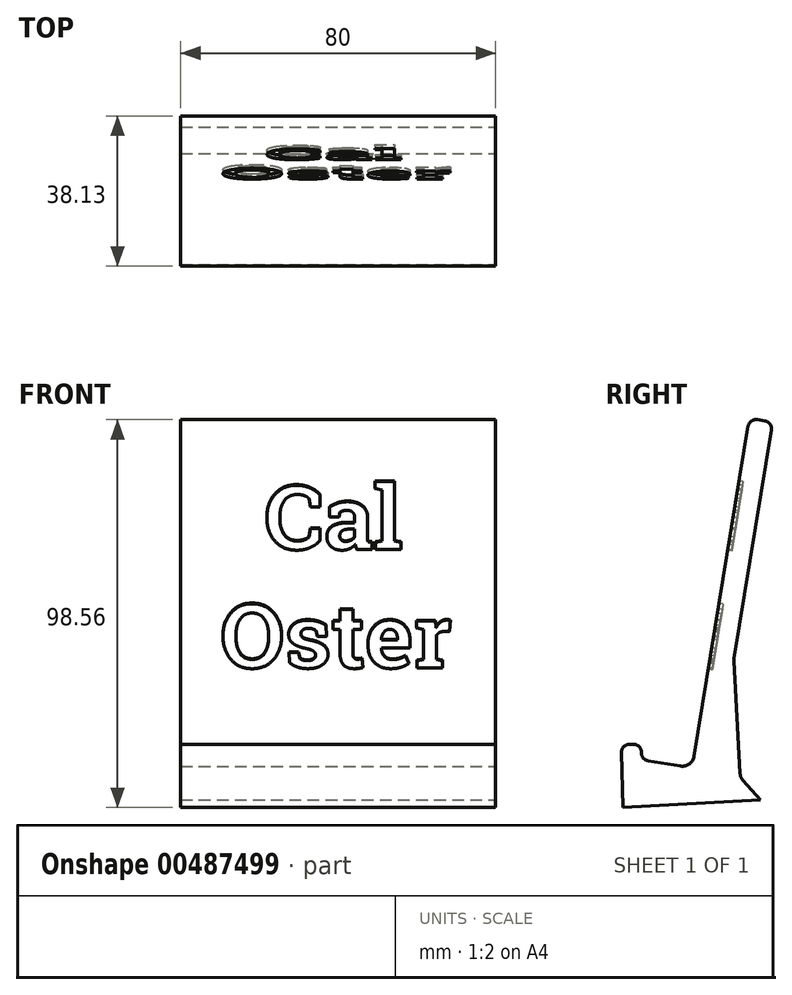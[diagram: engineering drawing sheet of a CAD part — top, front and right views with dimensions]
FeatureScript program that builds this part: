
annotation { "Feature Type Name" : "Feature", "Feature Type Description" : "" }
export const myFeature = defineFeature(function(context is Context, id is Id, definition is map)
    precondition{}
    {
        {
            var Q0;
            Q0=qCreatedBy(makeId("Right.planeOp"),FACE);
            var sketch = newSketch(context, id + "F0", { "sketchPlane" : qUnion([Q0])});
            skLineSegment(sketch, "E0", {"start": v(-4.82, -56.69) * mm, "end": v(-24.14, 31.22) * mm});
            skLineSegment(sketch, "E1", {"start": v(-4.82, -56.69) * mm, "end": v(7.88, -53.9) * mm});
            skLineSegment(sketch, "E2", {"start": v(7.88, -53.9) * mm, "end": v(7.88, -49.9) * mm});
            skLineSegment(sketch, "E3.0", {"start": v(-16.88, -29.77) * mm, "end": v(-30, 29.93) * mm});
            skLineSegment(sketch, "E4", {"start": v(-24.14, 31.22) * mm, "end": v(-30, 29.93) * mm});
            skLineSegment(sketch, "E5", {"start": v(7.88, -49.9) * mm, "end": v(12.88, -49.76) * mm});
            skLineSegment(sketch, "E6", {"start": v(-16.88, -29.77) * mm, "end": v(-16.88, -59.77) * mm});
            skLineSegment(sketch, "E7", {"start": v(12.88, -49.76) * mm, "end": v(13.31, -65.75) * mm});
            skLineSegment(sketch, "E8", {"start": v(-21.69, -65.75) * mm, "end": v(-16.88, -59.77) * mm});
            skLineSegment(sketch, "E9", {"start": v(13.31, -65.75) * mm, "end": v(-21.69, -65.75) * mm});
            skSolve(sketch);
        }
        {
            var Q0;
            Q0=makeQuery(id+"F0.imprint","IMPRINT",FACE,{"disambiguationData":[TD([[makeQuery(id+"F0.imprint","IMPRINT",EDGE,{"derivedFrom":sQuery(id+"F0.wireOp",EDGE,"E0")}),1.0]])]});
            extrude(context, id + "F1", {"entities" : qUnion([Q0]), "depth" : 80 * mm});
        }
        {
            var Q0;
            Q0=makeQuery(id+"F1.opExtrude","SWEPT_EDGE",EDGE,{"disambiguationData":[OSD([sQuery(id+"F0.wireOp",EDGE,"E3.0"),sQuery(id+"F0.wireOp",EDGE,"E4")])]});
            fillet(context, id + "F2", {"entities" : qUnion([Q0]), "radius" : 2 * mm, "tangentPropagation" : true, "allowEdgeOverflow" : false});
        }
        {
            var Q0;
            Q0=makeQuery(id+"F1.opExtrude","SWEPT_EDGE",EDGE,{"disambiguationData":[OSD([sQuery(id+"F0.wireOp",EDGE,"E0"),sQuery(id+"F0.wireOp",EDGE,"E4")])]});
            fillet(context, id + "F3", {"entities" : qUnion([Q0]), "radius" : 2 * mm, "tangentPropagation" : true, "allowEdgeOverflow" : false});
        }
        {
            var Q0;
            Q0=makeQuery(id+"F1.opExtrude","SWEPT_EDGE",EDGE,{"disambiguationData":[OSD([sQuery(id+"F0.wireOp",EDGE,"E0"),sQuery(id+"F0.wireOp",EDGE,"E1")])]});
            fillet(context, id + "F4", {"entities" : qUnion([Q0]), "radius" : 3 * mm, "tangentPropagation" : true, "allowEdgeOverflow" : false});
        }
        {
            var Q0;
            Q0=makeQuery(id+"F1.opExtrude","SWEPT_EDGE",EDGE,{"disambiguationData":[OSD([sQuery(id+"F0.wireOp",EDGE,"E1"),sQuery(id+"F0.wireOp",EDGE,"E2")])]});
            fillet(context, id + "F5", {"entities" : qUnion([Q0]), "radius" : 2 * mm, "tangentPropagation" : true, "allowEdgeOverflow" : false});
        }
        {
            var Q0;
            Q0=makeQuery(id+"F1.opExtrude","SWEPT_EDGE",EDGE,{"disambiguationData":[OSD([sQuery(id+"F0.wireOp",EDGE,"E5"),sQuery(id+"F0.wireOp",EDGE,"E7")])]});
            fillet(context, id + "F6", {"entities" : qUnion([Q0]), "radius" : 2 * mm, "tangentPropagation" : true, "allowEdgeOverflow" : false});
        }
        {
            var Q0;
            Q0=makeQuery(id+"F1.opExtrude","SWEPT_EDGE",EDGE,{"disambiguationData":[OSD([sQuery(id+"F0.wireOp",EDGE,"E2"),sQuery(id+"F0.wireOp",EDGE,"E5")])]});
            fillet(context, id + "F7", {"entities" : qUnion([Q0]), "radius" : 2 * mm, "tangentPropagation" : true, "allowEdgeOverflow" : false});
        }
        {
            var Q0;
            Q0=makeQuery(id+"F1.opExtrude","SWEPT_FACE",FACE,{"disambiguationData":[OSD([sQuery(id+"F0.wireOp",EDGE,"E0")])]});
            var sketch = newSketch(context, id + "F8", { "sketchPlane" : qUnion([Q0])});
            skText(sketch, "E10", { "text": "  Cal\nOster", "fontName": "RobotoSlab-Bold.ttf"});
            const initialGuessF8  = {"E10": [-0.07, 0.00196, 1, 0, 0.01663]};
            skSetInitialGuess(sketch, initialGuessF8);
            skSolve(sketch);
        }
        {
            var Q0;
            Q0 = qSketchRegion(id + "F8", true);
            extrude(context, id + "F9", {"entities" : qUnion([Q0]), "operationType" : NewBodyOperationType.REMOVE, "oppositeDirection" : true, "depth" : 1 * mm});
        }
        {
            var Q0;
            Q0=makeQuery(id+"F1.opExtrude","SWEPT_EDGE",EDGE,{"disambiguationData":[OSD([sQuery(id+"F0.wireOp",EDGE,"E3.0"),sQuery(id+"F0.wireOp",EDGE,"E6")])]});
            fillet(context, id + "F10", {"entities" : qUnion([Q0]), "radius" : 3 * mm, "tangentPropagation" : true, "allowEdgeOverflow" : false});
        }
        {
            var Q0;
            Q0=makeQuery(id+"F1.opExtrude","SWEPT_EDGE",EDGE,{"disambiguationData":[OSD([sQuery(id+"F0.wireOp",EDGE,"E6"),sQuery(id+"F0.wireOp",EDGE,"E8")])]});
            fillet(context, id + "F11", {"entities" : qUnion([Q0]), "radius" : 3 * mm, "tangentPropagation" : true, "allowEdgeOverflow" : false});
        }
        {
            var Q0;
            Q0=makeQuery(id+"F1.opExtrude","SWEPT_BODY",BODY,{"disambiguationData":[OSD([sQuery(id+"F0.wireOp",EDGE,"E0"),sQuery(id+"F0.wireOp",EDGE,"E1"),sQuery(id+"F0.wireOp",EDGE,"E2"),sQuery(id+"F0.wireOp",EDGE,"E3.0"),sQuery(id+"F0.wireOp",EDGE,"E4"),sQuery(id+"F0.wireOp",EDGE,"E5"),sQuery(id+"F0.wireOp",EDGE,"E6"),sQuery(id+"F0.wireOp",EDGE,"E7"),sQuery(id+"F0.wireOp",EDGE,"E8"),sQuery(id+"F0.wireOp",EDGE,"E9")])]});
            var Q1;
            Q1=makeQuery(id+"F1.opExtrude","CAP_EDGE",EDGE,{"disambiguationData":[OSD([sQuery(id+"F0.wireOp",EDGE,"E7")])],"isStart":true});
            transform(context, id + "F12", {"entities" : qUnion([Q0]), "transformType" : TransformType.ROTATION, "transformAxis" : qUnion([Q1]), "angle" : 180 * degree, "makeCopy" : false});
        }
        {
            var Q0;
            Q0=makeQuery(id+"F1.opExtrude","SWEPT_BODY",BODY,{"disambiguationData":[OSD([sQuery(id+"F0.wireOp",EDGE,"E0"),sQuery(id+"F0.wireOp",EDGE,"E1"),sQuery(id+"F0.wireOp",EDGE,"E2"),sQuery(id+"F0.wireOp",EDGE,"E3.0"),sQuery(id+"F0.wireOp",EDGE,"E4"),sQuery(id+"F0.wireOp",EDGE,"E5"),sQuery(id+"F0.wireOp",EDGE,"E6"),sQuery(id+"F0.wireOp",EDGE,"E7"),sQuery(id+"F0.wireOp",EDGE,"E8"),sQuery(id+"F0.wireOp",EDGE,"E9")])]});
            transform(context, id + "F13", {"entities" : qUnion([Q0]), "transformType" : TransformType.TRANSLATION_3D, "dx" : 40 * mm, "dy" : 0 * mm, "dz" : 0 * mm, "makeCopy" : false});
        }
        {
            var Q0;
            Q0=makeQuery(id+"F1.opExtrude","SWEPT_BODY",BODY,{"disambiguationData":[OSD([sQuery(id+"F0.wireOp",EDGE,"E0"),sQuery(id+"F0.wireOp",EDGE,"E1"),sQuery(id+"F0.wireOp",EDGE,"E2"),sQuery(id+"F0.wireOp",EDGE,"E3.0"),sQuery(id+"F0.wireOp",EDGE,"E4"),sQuery(id+"F0.wireOp",EDGE,"E5"),sQuery(id+"F0.wireOp",EDGE,"E6"),sQuery(id+"F0.wireOp",EDGE,"E7"),sQuery(id+"F0.wireOp",EDGE,"E8"),sQuery(id+"F0.wireOp",EDGE,"E9")])]});
            transform(context, id + "F14", {"entities" : qUnion([Q0]), "transformType" : TransformType.TRANSLATION_3D, "dx" : 0 * mm, "dy" : -40 * mm, "dz" : 0 * mm, "makeCopy" : false});
        }
    });
